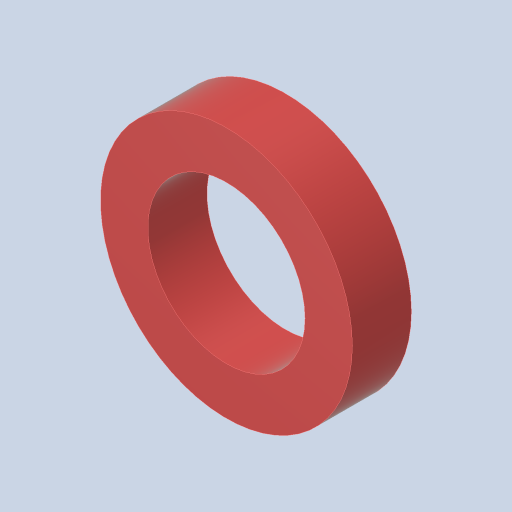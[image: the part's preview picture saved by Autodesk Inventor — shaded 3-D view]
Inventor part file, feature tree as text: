
AUTODESK INVENTOR PART (.ipt)
format: ipt  version: 2023.4 (Build 274418000, 418)  size: 113,152 bytes
history: native  units: in
note: dims shown in document units (in); Inventor stores cm internally (conversion verified against a paired STEP export)
features: extrude x1, sketch x1
ambient origin geometry x8: Origin, YZ Plane, XZ Plane, XY Plane, X Axis, Y Axis, Z Axis, Center Point
bodies: Solid1 (feature_tree)
feature tree (2):
  extrude  "Extrusion1"  Depth=0.156in
  sketch  "Sketch1"  dims[d0=0.415in d1=0.125in d2=0.156in d3=0.0in]
